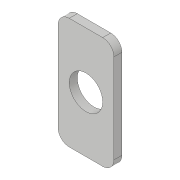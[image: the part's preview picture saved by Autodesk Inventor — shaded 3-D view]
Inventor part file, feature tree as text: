
AUTODESK INVENTOR PART (.ipt)
format: ipt  version: 2022 (Build 260153000, 153)  size: 136,704 bytes
history: native  units: mm
features: extrude x2, sketch x2, projected_geometry x1
ambient origin geometry x8: Origin, YZ Plane, XZ Plane, XY Plane, X Axis, Y Axis, Z Axis, Center Point
bodies: Solid1 (feature_tree)
feature tree (5):
  extrude  "Extrusion1"  Depth=3.0mm
  extrude  "Extrusion2"  Depth=0.6mm
  sketch  "Sketch1"  dims[d4=3.0mm d5=0.0mm d6=40.0mm]
  sketch  "Skizze2"  dims[d7=8.1mm d8=8.1mm d9=25.0mm d10=50.0mm d11=5.0mm d12=15.0mm d13=0.6mm d14=0.0mm]
  projected_geometry  "Projizierte Kontur1"
